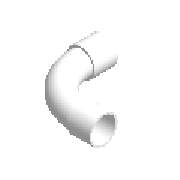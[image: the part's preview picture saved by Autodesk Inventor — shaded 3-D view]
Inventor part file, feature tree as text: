
AUTODESK INVENTOR PART (.ipt)
format: ipt  version: 2023 (Build 270158000, 158)  size: 222,720 bytes
history: native  units: mm (DEFAULTED — no unit token found)
features: other x6, sketch x2, revolve x2, sweep x1
ambient origin geometry x8: Origin, YZ Plane, XZ Plane, XY Plane, X Axis, Y Axis, Z Axis, Center Point
bodies: Solid1 (feature_tree)
feature tree (11):
  sketch  "Sketch1"  dims[d3=90.0deg d0=110.0mm]
  revolve  "Revolution1"  [1 undecoded]
  sweep  "Sweep1"
  revolve  "Revolution2"  [1 undecoded]
  other  "Work Point18"
  other  "Work Point19"
  other  "Work Axis30"
  other  "Work Point20"
  other  "Work Axis31"
  other  "Work Point21"
  sketch  "Sketch2"  dims[d1=8.2mm d2=61.0mm d4=93.6mm d5=0.0mm d6=110.0mm d7=93.6mm d8=211.8mm d9=211.8mm d160=90.0deg d10=8.2mm d11=8.2mm d12=61.0mm d13=110.0mm d14=220.0mm d15=220.0mm d16=8.2mm d192=0.0mm]
note: 2 required parameter values undecoded (feature->parameter linkage not recoverable at this tier; creation-order binding heuristic only, values carry confidence <= 0.55)
